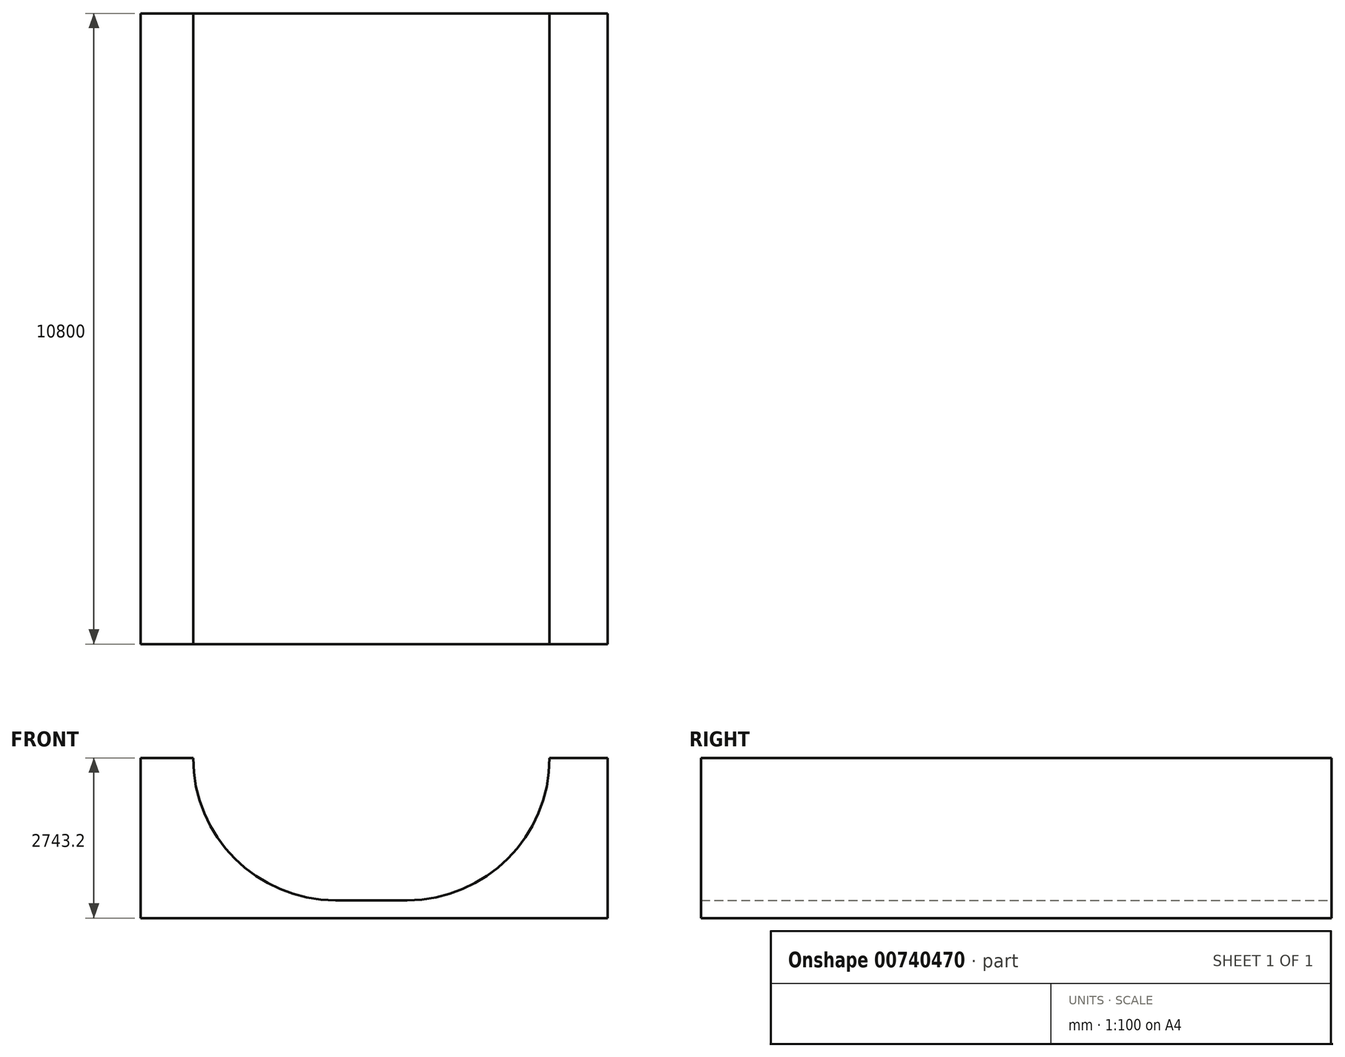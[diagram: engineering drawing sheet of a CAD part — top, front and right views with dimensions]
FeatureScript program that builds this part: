
annotation { "Feature Type Name" : "Feature", "Feature Type Description" : "" }
export const myFeature = defineFeature(function(context is Context, id is Id, definition is map)
    precondition{}
    {
        {
            var Q0;
            Q0=qCreatedBy(makeId("Front.planeOp"),FACE);
            var sketch = newSketch(context, id + "F0", { "sketchPlane" : qUnion([Q0])});
            skLineSegment(sketch, "E0", {"start": v(0, 0) * mm, "end": v(8000, 0) * mm});
            skLineSegment(sketch, "E1", {"start": v(0, 0) * mm, "end": v(0, 2743.2) * mm});
            skLineSegment(sketch, "E2", {"start": v(8000, 0) * mm, "end": v(8000, 2743.2) * mm});
            skLineSegment(sketch, "E3", {"start": v(8000, 2743.2) * mm, "end": v(0, 2743.2) * mm});
            skLineSegment(sketch, "E4", {"start": v(0, 304.8) * mm, "end": v(8000, 304.8) * mm});
            skLineSegment(sketch, "E5", {"start": v(0, 2743.2) * mm, "end": v(8000, 2743.2) * mm});
            skArc(sketch, "E6", {"start": v(897.82, 2743.2) * mm, "mid": v(1612, 1019) * mm, "end": v(3336.22, 304.8) * mm});
            skArc(sketch, "E7", {"start": v(4567.57, 304.8) * mm, "mid": v(6291.78, 1019) * mm, "end": v(7005.97, 2743.2) * mm});
            skLineSegment(sketch, "E8", {"start": v(3336.22, 304.8) * mm, "end": v(4567.57, 304.8) * mm});
            skSolve(sketch);
        }
        {
            var Q0;
            {var subQ5=sQuery(id+"F0.wireOp",EDGE,"E6");Q0=makeQuery(id+"F0.imprint","IMPRINT",FACE,{"disambiguationData":[TD([[makeQuery(id+"F0.imprint","IMPRINT",EDGE,{"derivedFrom":subQ5}),-1.0]])]});}
            var Q1;
            {var subQ1=sQuery(id+"F0.wireOp",EDGE,"E0");Q1=makeQuery(id+"F0.imprint","IMPRINT",FACE,{"disambiguationData":[TD([[makeQuery(id+"F0.imprint","IMPRINT",EDGE,{"derivedFrom":subQ1}),1.0]])]});}
            var Q2;
            {var subQ5=sQuery(id+"F0.wireOp",EDGE,"E7");Q2=makeQuery(id+"F0.imprint","IMPRINT",FACE,{"disambiguationData":[TD([[makeQuery(id+"F0.imprint","IMPRINT",EDGE,{"derivedFrom":subQ5}),-1.0]])]});}
            extrude(context, id + "F1", {"entities" : qUnion([Q0, Q1, Q2]), "depth" : 10800 * mm, "offsetDistance" : 25 * mm});
        }
    });
